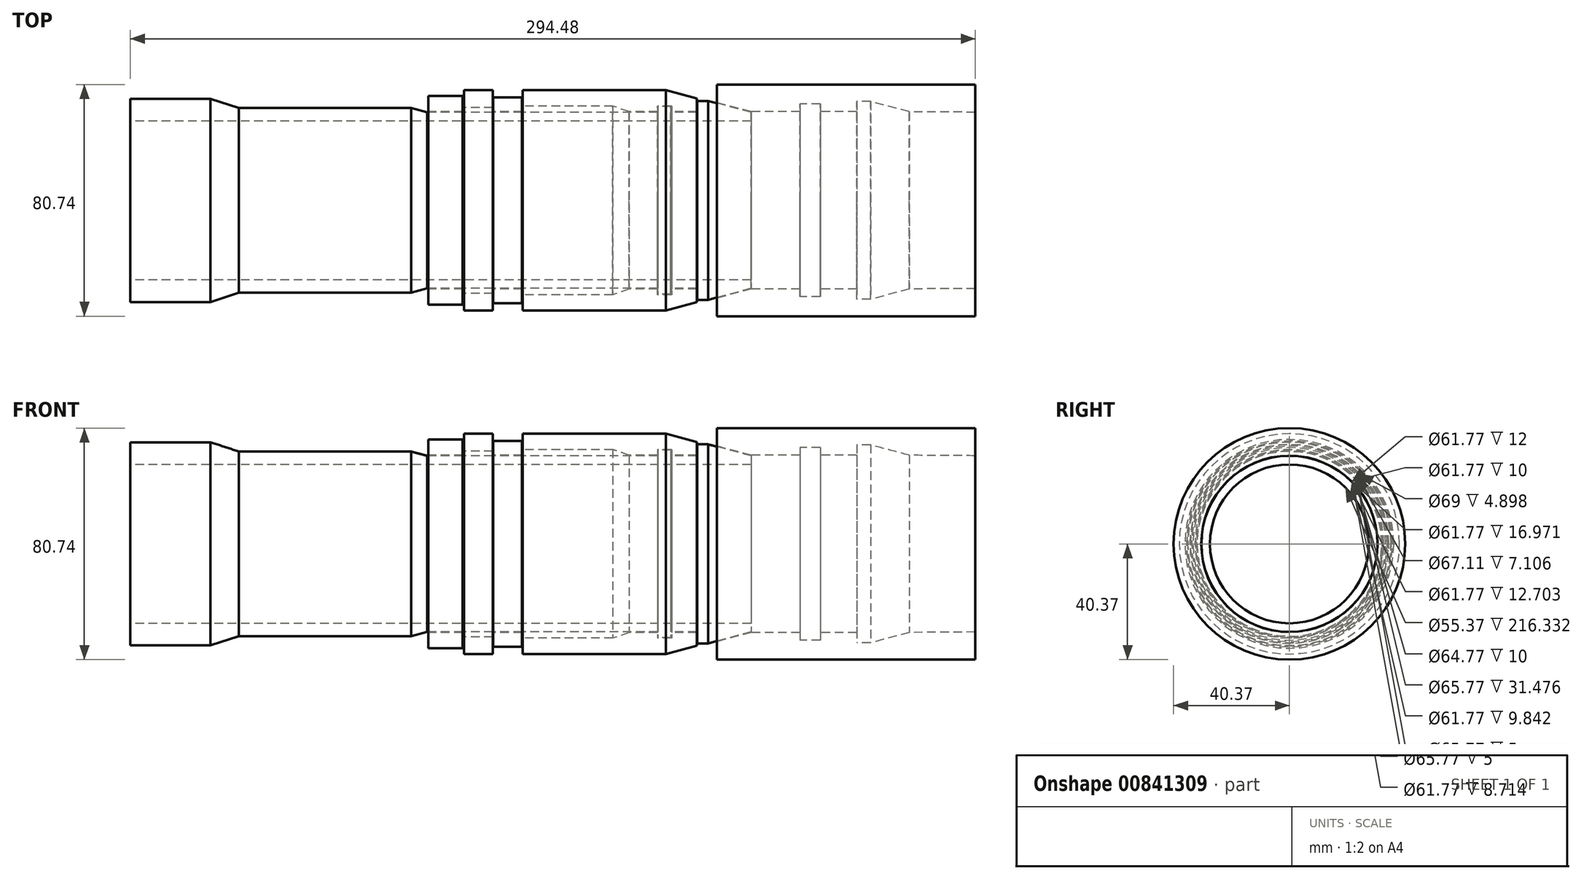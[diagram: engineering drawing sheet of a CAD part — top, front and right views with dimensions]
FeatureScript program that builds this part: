
annotation { "Feature Type Name" : "Feature", "Feature Type Description" : "" }
export const myFeature = defineFeature(function(context is Context, id is Id, definition is map)
    precondition{}
    {
        {
            var Q0;
            Q0=qCreatedBy(makeId("Front.planeOp"),FACE);
            var sketch = newSketch(context, id + "F0", { "sketchPlane" : qUnion([Q0])});
            skLineSegment(sketch, "E0", {"start": v(27.92, 35.42) * mm, "end": v(0, 35.42) * mm});
            skLineSegment(sketch, "E1", {"start": v(0, 35.42) * mm, "end": v(0, 27.69) * mm});
            skLineSegment(sketch, "E2", {"start": v(37.86, 32.19) * mm, "end": v(27.92, 35.42) * mm});
            skLineSegment(sketch, "E3", {"start": v(37.86, 32.19) * mm, "end": v(97.86, 32.19) * mm});
            skLineSegment(sketch, "E4", {"start": v(0, 27.69) * mm, "end": v(216.33, 27.69) * mm});
            skLineSegment(sketch, "E5", {"start": v(0, 0) * mm, "end": v(186.5, 0) * mm});
            skLineSegment(sketch, "E6.bottom", {"start": v(126.5, 35.89) * mm, "end": v(136.5, 35.89) * mm});
            skLineSegment(sketch, "E6.top", {"start": v(126.5, 30.89) * mm, "end": v(136.5, 30.89) * mm});
            skLineSegment(sketch, "E6.left", {"start": v(126.5, 35.89) * mm, "end": v(126.5, 30.89) * mm});
            skLineSegment(sketch, "E6.right", {"start": v(136.5, 35.89) * mm, "end": v(136.5, 30.89) * mm});
            skLineSegment(sketch, "E7.bottom", {"start": v(136.7, 38.39) * mm, "end": v(186.7, 38.39) * mm});
            skLineSegment(sketch, "E7.top", {"start": v(136.7, 32.89) * mm, "end": v(168.18, 32.89) * mm});
            skLineSegment(sketch, "E7.left", {"start": v(136.7, 38.39) * mm, "end": v(136.7, 32.89) * mm});
            skLineSegment(sketch, "E7.right", {"start": v(197.4, 35.52) * mm, "end": v(197.4, 30.89) * mm});
            skLineSegment(sketch, "E8.bottom", {"start": v(103.8, 36.39) * mm, "end": v(115.8, 36.39) * mm});
            skLineSegment(sketch, "E8.top", {"start": v(103.8, 30.89) * mm, "end": v(115.8, 30.89) * mm});
            skLineSegment(sketch, "E8.left", {"start": v(103.8, 36.39) * mm, "end": v(103.8, 30.89) * mm});
            skLineSegment(sketch, "E8.right", {"start": v(115.8, 36.39) * mm, "end": v(115.8, 30.89) * mm});
            skLineSegment(sketch, "E9", {"start": v(97.86, 32.19) * mm, "end": v(103.46, 30.69) * mm});
            skLineSegment(sketch, "E10", {"start": v(183.84, 30.69) * mm, "end": v(103.46, 30.69) * mm});
            skLineSegment(sketch, "E11", {"start": v(116.3, 32.39) * mm, "end": v(126.3, 32.39) * mm});
            skLineSegment(sketch, "E12", {"start": v(116.3, 32.39) * mm, "end": v(116.3, 38.39) * mm});
            skLineSegment(sketch, "E13", {"start": v(116.3, 38.39) * mm, "end": v(126.3, 38.39) * mm});
            skLineSegment(sketch, "E14", {"start": v(126.3, 38.39) * mm, "end": v(126.3, 32.39) * mm});
            skLineSegment(sketch, "E15", {"start": v(183.84, 30.69) * mm, "end": v(183.84, 32.69) * mm});
            skLineSegment(sketch, "E16", {"start": v(183.84, 32.69) * mm, "end": v(188.34, 32.69) * mm});
            skLineSegment(sketch, "E17", {"start": v(188.34, 32.69) * mm, "end": v(188.34, 30.69) * mm});
            skLineSegment(sketch, "E18", {"start": v(188.34, 30.69) * mm, "end": v(197.6, 30.69) * mm});
            skLineSegment(sketch, "E19", {"start": v(183.69, 32.89) * mm, "end": v(188.69, 32.89) * mm});
            skLineSegment(sketch, "E20", {"start": v(186.7, 38.39) * mm, "end": v(197.4, 35.52) * mm});
            skLineSegment(sketch, "E21", {"start": v(168.18, 32.89) * mm, "end": v(173.85, 30.89) * mm});
            skLineSegment(sketch, "E22", {"start": v(173.85, 30.89) * mm, "end": v(183.69, 30.89) * mm});
            skPoint(sketch, "E23", {"position": v(183.84, 31.69) * mm});
            skLineSegment(sketch, "E24", {"start": v(183.69, 32.89) * mm, "end": v(183.69, 30.89) * mm});
            skLineSegment(sketch, "E25", {"start": v(188.69, 32.89) * mm, "end": v(188.69, 30.89) * mm});
            skLineSegment(sketch, "E26", {"start": v(188.69, 30.89) * mm, "end": v(197.4, 30.89) * mm});
            skLineSegment(sketch, "E27", {"start": v(197.6, 30.69) * mm, "end": v(197.6, 34.69) * mm});
            skLineSegment(sketch, "E28", {"start": v(197.6, 34.69) * mm, "end": v(201.4, 34.69) * mm});
            skLineSegment(sketch, "E29", {"start": v(201.4, 34.69) * mm, "end": v(216.33, 30.69) * mm});
            skLineSegment(sketch, "E30", {"start": v(216.33, 30.69) * mm, "end": v(216.33, 27.69) * mm});
            skLineSegment(sketch, "E31", {"start": v(204.46, 40.37) * mm, "end": v(294.48, 40.37) * mm});
            skLineSegment(sketch, "E32", {"start": v(204.46, 40.37) * mm, "end": v(204.46, 34.08) * mm});
            skLineSegment(sketch, "E33", {"start": v(204.46, 34.08) * mm, "end": v(216.36, 30.89) * mm});
            skLineSegment(sketch, "E34", {"start": v(216.36, 30.89) * mm, "end": v(233.33, 30.89) * mm});
            skLineSegment(sketch, "E35", {"start": v(233.33, 30.89) * mm, "end": v(233.33, 33.55) * mm});
            skLineSegment(sketch, "E36", {"start": v(233.33, 33.55) * mm, "end": v(240.43, 33.55) * mm});
            skLineSegment(sketch, "E37", {"start": v(240.43, 33.55) * mm, "end": v(240.43, 30.89) * mm});
            skLineSegment(sketch, "E38", {"start": v(253.14, 30.89) * mm, "end": v(253.14, 34.5) * mm});
            skLineSegment(sketch, "E39", {"start": v(253.14, 34.5) * mm, "end": v(258.04, 34.5) * mm});
            skLineSegment(sketch, "E40", {"start": v(258.04, 34.5) * mm, "end": v(271.51, 30.89) * mm});
            skLineSegment(sketch, "E41", {"start": v(294.48, 40.37) * mm, "end": v(294.48, 30.72) * mm});
            skLineSegment(sketch, "E42", {"start": v(294.48, 30.72) * mm, "end": v(271.51, 30.89) * mm});
            skLineSegment(sketch, "E43.trimOffspring", {"start": v(240.43, 30.89) * mm, "end": v(253.14, 30.89) * mm});
            skSolve(sketch);
        }
        {
            var Q0;
            Q0 = qSketchRegion(id + "F0", true);
            var Q1;
            Q1=sQuery(id+"F0.wireOp",EDGE,"E5");
            revolve(context, id + "F1", {"surfaceOperationType" : NewSurfaceOperationType.NEW, "entities" : qUnion([Q0]), "axis" : qUnion([Q1]), "revolveType" : RevolveType.FULL});
        }
    });
